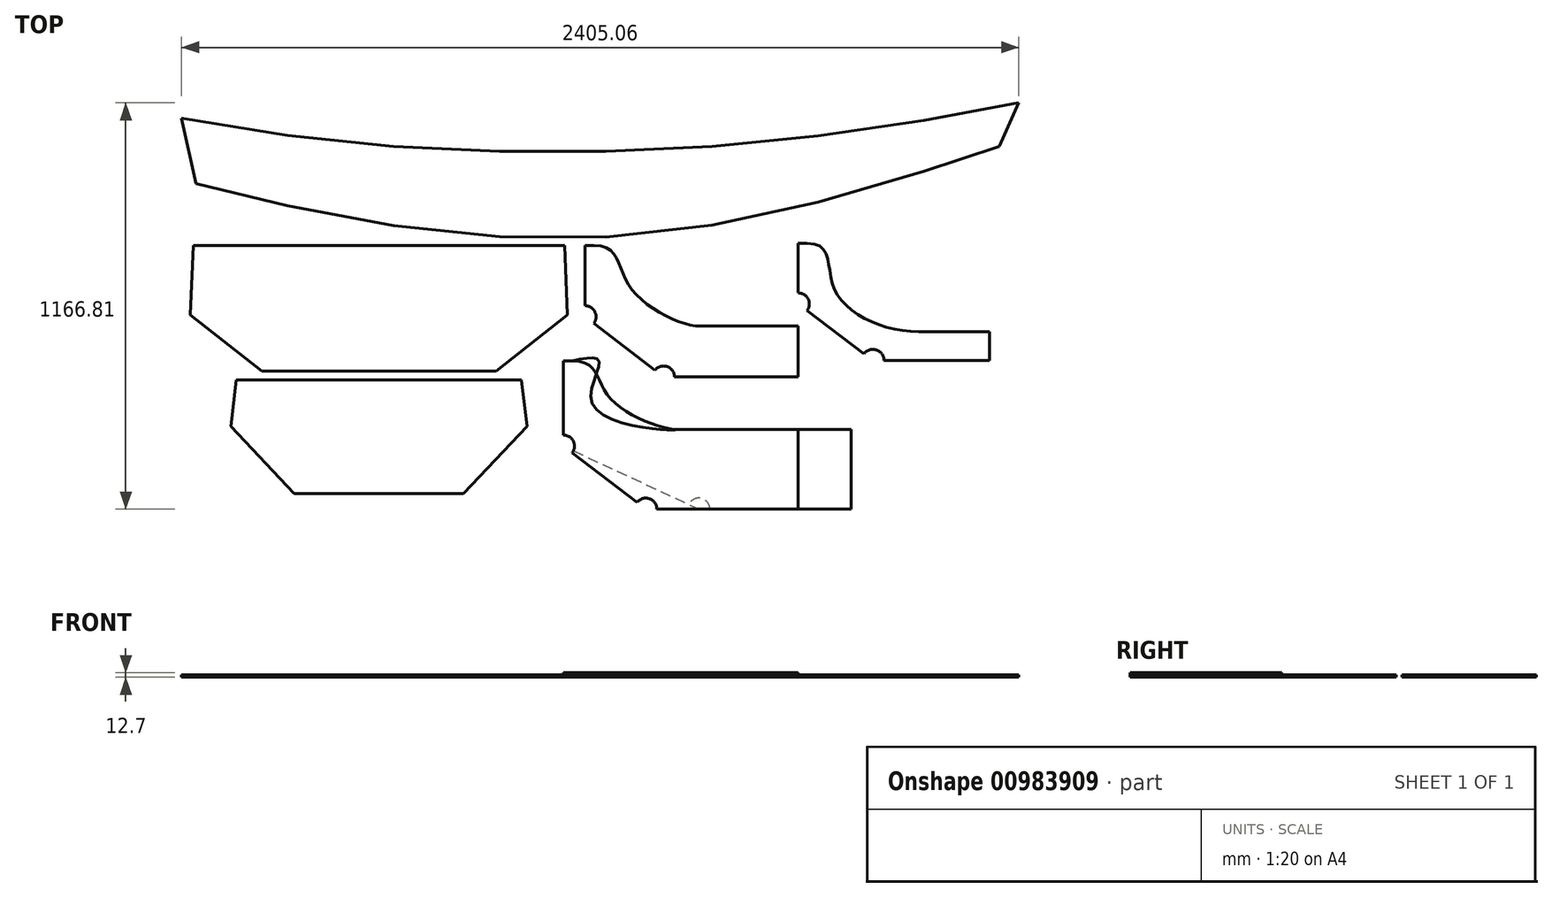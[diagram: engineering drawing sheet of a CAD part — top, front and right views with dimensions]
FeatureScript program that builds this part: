
annotation { "Feature Type Name" : "Feature", "Feature Type Description" : "" }
export const myFeature = defineFeature(function(context is Context, id is Id, definition is map)
    precondition{}
    {
        {
            var Q0;
            Q0=qCreatedBy(makeId("Top.planeOp"),FACE);
            var sketch = newSketch(context, id + "F0", { "sketchPlane" : qUnion([Q0])});
            skLineSegment(sketch, "E0.bottom", {"start": v(2438.4, -1219.2) * mm, "end": v(0, -1219.2) * mm});
            skLineSegment(sketch, "E0.top", {"start": v(2438.4, 0) * mm, "end": v(0, 0) * mm});
            skLineSegment(sketch, "E0.left", {"start": v(2438.4, -1219.2) * mm, "end": v(2438.4, 0) * mm});
            skLineSegment(sketch, "E0.right", {"start": v(0, -1219.2) * mm, "end": v(0, 0) * mm});
            skPoint(sketch, "E1", {"position": v(0, -44.45) * mm});
            skPoint(sketch, "E2", {"position": v(304.8, -93.66) * mm});
            skPoint(sketch, "E3", {"position": v(609.6, -125.41) * mm});
            skPoint(sketch, "E4", {"position": v(914.4, -139.7) * mm});
            skPoint(sketch, "E5", {"position": v(1219.2, -139.7) * mm});
            skPoint(sketch, "E6", {"position": v(1524, -125.41) * mm});
            skPoint(sketch, "E7", {"position": v(1828.8, -95.25) * mm});
            skPoint(sketch, "E8", {"position": v(2133.6, -50.8) * mm});
            skPoint(sketch, "E9", {"position": v(2405.06, 0) * mm});
            skLineSegment(sketch, "E10", {"start": v(2405.06, 0) * mm, "end": v(2133.6, -50.8) * mm});
            skLineSegment(sketch, "E11", {"start": v(1828.8, -95.25) * mm, "end": v(2133.6, -50.8) * mm});
            skLineSegment(sketch, "E12", {"start": v(1828.8, -95.25) * mm, "end": v(1524, -125.41) * mm});
            skLineSegment(sketch, "E13", {"start": v(1524, -125.41) * mm, "end": v(1219.2, -139.7) * mm});
            skLineSegment(sketch, "E14", {"start": v(914.4, -139.7) * mm, "end": v(1219.2, -139.7) * mm});
            skLineSegment(sketch, "E15", {"start": v(609.6, -125.41) * mm, "end": v(914.4, -139.7) * mm});
            skLineSegment(sketch, "E16", {"start": v(0, -44.45) * mm, "end": v(304.8, -93.66) * mm});
            skLineSegment(sketch, "E17", {"start": v(609.6, -125.41) * mm, "end": v(304.8, -93.66) * mm});
            skLineSegment(sketch, "E18", {"start": v(387.35, -102.26) * mm, "end": v(387.35, -310.75) * mm, "construction": true});
            skLineSegment(sketch, "E19", {"start": v(1079.5, -139.7) * mm, "end": v(1079.5, -385.03) * mm, "construction": true});
            skLineSegment(sketch, "E20", {"start": v(1909.76, -83.44) * mm, "end": v(1909.76, -262.14) * mm, "construction": true});
            skPoint(sketch, "E21", {"position": v(304.8, -295.27) * mm});
            skPoint(sketch, "E22", {"position": v(609.6, -352.42) * mm});
            skPoint(sketch, "E23", {"position": v(914.4, -384.17) * mm});
            skPoint(sketch, "E24", {"position": v(1219.2, -385.76) * mm});
            skPoint(sketch, "E25", {"position": v(1524, -350.84) * mm});
            skPoint(sketch, "E26", {"position": v(1828.8, -285.75) * mm});
            skPoint(sketch, "E27", {"position": v(2133.6, -196.85) * mm});
            skPoint(sketch, "E28", {"position": v(2349.5, -124.88) * mm});
            skPoint(sketch, "E29", {"position": v(41.27, -232.14) * mm});
            skPoint(sketch, "E30", {"position": v(0, -222.25) * mm});
            skLineSegment(sketch, "E31", {"start": v(304.8, -295.27) * mm, "end": v(609.6, -352.42) * mm});
            skLineSegment(sketch, "E32", {"start": v(609.6, -352.42) * mm, "end": v(914.4, -384.17) * mm});
            skLineSegment(sketch, "E33", {"start": v(914.4, -384.17) * mm, "end": v(1219.2, -385.76) * mm});
            skLineSegment(sketch, "E34", {"start": v(1219.2, -385.76) * mm, "end": v(1524, -350.84) * mm});
            skLineSegment(sketch, "E35", {"start": v(1524, -350.84) * mm, "end": v(1828.8, -285.75) * mm});
            skLineSegment(sketch, "E36", {"start": v(1828.8, -285.75) * mm, "end": v(2133.6, -196.85) * mm});
            skLineSegment(sketch, "E37", {"start": v(2133.6, -196.85) * mm, "end": v(2349.5, -124.88) * mm});
            skLineSegment(sketch, "E38", {"start": v(2349.5, -124.88) * mm, "end": v(2405.06, 0) * mm});
            skLineSegment(sketch, "E39.bottom", {"start": v(0, -1524) * mm, "end": v(2438.4, -1524) * mm});
            skLineSegment(sketch, "E39.top", {"start": v(0, -2743.2) * mm, "end": v(2438.4, -2743.2) * mm});
            skLineSegment(sketch, "E39.left", {"start": v(0, -1524) * mm, "end": v(0, -2743.2) * mm});
            skLineSegment(sketch, "E39.right", {"start": v(2438.4, -1524) * mm, "end": v(2438.4, -2743.2) * mm});
            skLineSegment(sketch, "E40", {"start": v(0, -1852.61) * mm, "end": v(2220.91, -1852.61) * mm, "construction": true});
            skPoint(sketch, "E41", {"position": v(0, -1665.29) * mm});
            skPoint(sketch, "E42", {"position": v(304.8, -1616.08) * mm});
            skPoint(sketch, "E43", {"position": v(609.6, -1581.15) * mm});
            skPoint(sketch, "E44", {"position": v(914.4, -1549.4) * mm});
            skPoint(sketch, "E45", {"position": v(1219.2, -1573.21) * mm});
            skPoint(sketch, "E46", {"position": v(1828.8, -1665.29) * mm});
            skPoint(sketch, "E47", {"position": v(1524, -1604.96) * mm});
            skLineSegment(sketch, "E48", {"start": v(0, -2005.01) * mm, "end": v(940, -2005.01) * mm, "construction": true});
            skPoint(sketch, "E49", {"position": v(2133.6, -1733.55) * mm});
            skPoint(sketch, "E50", {"position": v(2220.91, -1757.36) * mm});
            skPoint(sketch, "E51.MirrorP", {"position": v(0, -2344.74) * mm});
            skPoint(sketch, "E52.MirrorP", {"position": v(304.8, -2393.95) * mm});
            skPoint(sketch, "E53.MirrorP", {"position": v(609.6, -2428.87) * mm});
            skPoint(sketch, "E54.MirrorP", {"position": v(914.4, -2460.62) * mm});
            skPoint(sketch, "E55.MirrorP", {"position": v(1219.2, -2436.81) * mm});
            skPoint(sketch, "E56.MirrorP", {"position": v(1524, -2405.06) * mm});
            skPoint(sketch, "E57.MirrorP", {"position": v(1828.8, -2344.74) * mm});
            skPoint(sketch, "E58.MirrorP", {"position": v(2133.6, -2276.47) * mm});
            skPoint(sketch, "E59.MirrorP", {"position": v(2220.91, -2252.66) * mm});
            skLineSegment(sketch, "E60", {"start": v(0, -1665.29) * mm, "end": v(304.8, -1616.08) * mm});
            skLineSegment(sketch, "E61", {"start": v(304.8, -1616.08) * mm, "end": v(609.6, -1581.15) * mm});
            skLineSegment(sketch, "E62", {"start": v(609.6, -1581.15) * mm, "end": v(914.4, -1549.4) * mm});
            skLineSegment(sketch, "E63", {"start": v(914.4, -1549.4) * mm, "end": v(1219.2, -1573.21) * mm});
            skLineSegment(sketch, "E64", {"start": v(1524, -1604.96) * mm, "end": v(1219.2, -1573.21) * mm});
            skLineSegment(sketch, "E65", {"start": v(1828.8, -1665.29) * mm, "end": v(1524, -1604.96) * mm});
            skLineSegment(sketch, "E66", {"start": v(2133.6, -1733.55) * mm, "end": v(1828.8, -1665.29) * mm});
            skLineSegment(sketch, "E67", {"start": v(2220.91, -1757.36) * mm, "end": v(2133.6, -1733.55) * mm});
            skLineSegment(sketch, "E68", {"start": v(2220.91, -1757.36) * mm, "end": v(2220.91, -2252.66) * mm});
            skLineSegment(sketch, "E69", {"start": v(2133.6, -2276.47) * mm, "end": v(2220.91, -2252.66) * mm});
            skLineSegment(sketch, "E70", {"start": v(2133.6, -2276.47) * mm, "end": v(1828.8, -2344.74) * mm});
            skLineSegment(sketch, "E71", {"start": v(1524, -2405.06) * mm, "end": v(1828.8, -2344.74) * mm});
            skLineSegment(sketch, "E72", {"start": v(1524, -2405.06) * mm, "end": v(1219.2, -2436.81) * mm});
            skLineSegment(sketch, "E73", {"start": v(1219.2, -2436.81) * mm, "end": v(914.4, -2460.62) * mm});
            skLineSegment(sketch, "E74", {"start": v(914.4, -2460.62) * mm, "end": v(609.6, -2428.87) * mm});
            skLineSegment(sketch, "E75", {"start": v(609.6, -2428.87) * mm, "end": v(304.8, -2393.95) * mm});
            skLineSegment(sketch, "E76", {"start": v(304.8, -2393.95) * mm, "end": v(0, -2344.74) * mm});
            skLineSegment(sketch, "E77", {"start": v(33.34, -409.57) * mm, "end": v(25.4, -609.6) * mm});
            skLineSegment(sketch, "E78", {"start": v(25.4, -609.6) * mm, "end": v(230.19, -769.94) * mm});
            skLineSegment(sketch, "E79", {"start": v(230.19, -769.94) * mm, "end": v(566.74, -769.94) * mm});
            skLineSegment(sketch, "E80", {"start": v(566.74, -769.94) * mm, "end": v(566.74, -409.57) * mm, "construction": true});
            skLineSegment(sketch, "E81", {"start": v(414.34, -769.94) * mm, "end": v(414.34, -409.57) * mm, "construction": true});
            skLineSegment(sketch, "E82", {"start": v(33.34, -409.57) * mm, "end": v(566.74, -409.57) * mm});
            skLineSegment(sketch, "E83.MirrorCS", {"start": v(1100.14, -409.57) * mm, "end": v(1108.08, -609.6) * mm});
            skLineSegment(sketch, "E84.MirrorCS", {"start": v(1108.08, -609.6) * mm, "end": v(903.29, -769.94) * mm});
            skLineSegment(sketch, "E85.MirrorCS", {"start": v(903.29, -769.94) * mm, "end": v(566.74, -769.94) * mm});
            skLineSegment(sketch, "E86.MirrorCS", {"start": v(1100.14, -409.57) * mm, "end": v(566.74, -409.57) * mm});
            skLineSegment(sketch, "E87", {"start": v(566.74, -795.34) * mm, "end": v(157.16, -795.34) * mm});
            skLineSegment(sketch, "E88", {"start": v(157.16, -795.34) * mm, "end": v(141.29, -928.69) * mm});
            skLineSegment(sketch, "E89", {"start": v(141.29, -928.69) * mm, "end": v(323.85, -1122.36) * mm});
            skLineSegment(sketch, "E90", {"start": v(323.85, -1122.36) * mm, "end": v(566.74, -1122.36) * mm});
            skLineSegment(sketch, "E91.MirrorCS", {"start": v(809.62, -1122.36) * mm, "end": v(566.74, -1122.36) * mm});
            skLineSegment(sketch, "E92.MirrorCS", {"start": v(992.19, -928.69) * mm, "end": v(809.62, -1122.36) * mm});
            skLineSegment(sketch, "E93.MirrorCS", {"start": v(976.31, -795.34) * mm, "end": v(992.19, -928.69) * mm});
            skLineSegment(sketch, "E94.MirrorCS", {"start": v(566.74, -795.34) * mm, "end": v(976.31, -795.34) * mm});
            skLineSegment(sketch, "E95", {"start": v(41.27, -232.14) * mm, "end": v(0, -44.45) * mm});
            skLineSegment(sketch, "E96", {"start": v(0, -222.25) * mm, "end": v(41.27, -232.14) * mm, "construction": true});
            skLineSegment(sketch, "E97", {"start": v(41.27, -232.14) * mm, "end": v(304.8, -295.27) * mm});
            skLineSegment(sketch, "E98", {"start": v(2349.5, -124.88) * mm, "end": v(2405.06, -106.36) * mm, "construction": true});
            skLineSegment(sketch, "E99", {"start": v(1158.88, -409.57) * mm, "end": v(1158.88, -614.36) * mm});
            skLineSegment(sketch, "E100", {"start": v(1158.88, -614.36) * mm, "end": v(1384.3, -787.4) * mm});
            skLineSegment(sketch, "E101", {"start": v(1384.3, -787.4) * mm, "end": v(1771.65, -787.4) * mm});
            skLineSegment(sketch, "E102", {"start": v(1619.25, -582.61) * mm, "end": v(1619.25, -787.4) * mm, "construction": true});
            skLineSegment(sketch, "E103", {"start": v(1771.65, -787.4) * mm, "end": v(1771.65, -641.35) * mm});
            skLineSegment(sketch, "E104", {"start": v(1771.65, -641.35) * mm, "end": v(1489.08, -641.35) * mm});
            skLineSegment(sketch, "E105", {"start": v(1184.28, -409.57) * mm, "end": v(1158.88, -409.57) * mm});
            skLineSegment(sketch, "E106", {"start": v(1771.65, -1166.81) * mm, "end": v(1333.5, -1166.81) * mm});
            skLineSegment(sketch, "E107", {"start": v(1333.5, -1166.81) * mm, "end": v(1096.96, -985.84) * mm});
            skLineSegment(sketch, "E108", {"start": v(1096.96, -985.84) * mm, "end": v(1096.96, -741.36) * mm});
            skLineSegment(sketch, "E109", {"start": v(1771.65, -1166.81) * mm, "end": v(1771.65, -938.21) * mm});
            skLineSegment(sketch, "E110", {"start": v(1771.65, -938.21) * mm, "end": v(1427.16, -938.21) * mm});
            skLineSegment(sketch, "E111", {"start": v(1122.36, -741.36) * mm, "end": v(1096.96, -741.36) * mm});
            skLineSegment(sketch, "E112", {"start": v(1771.65, -403.06) * mm, "end": v(1771.65, -577.68) * mm});
            skLineSegment(sketch, "E113", {"start": v(1771.65, -577.68) * mm, "end": v(1985.96, -739.6) * mm});
            skLineSegment(sketch, "E114", {"start": v(1985.96, -739.6) * mm, "end": v(2320.93, -739.6) * mm});
            skLineSegment(sketch, "E115", {"start": v(2168.53, -739.6) * mm, "end": v(2168.53, -479.2) * mm, "construction": true});
            skLineSegment(sketch, "E116", {"start": v(2320.93, -739.6) * mm, "end": v(2320.93, -657.06) * mm});
            skLineSegment(sketch, "E117", {"start": v(2320.93, -657.06) * mm, "end": v(2117.72, -657.06) * mm});
            skLineSegment(sketch, "E118", {"start": v(1797.05, -403.06) * mm, "end": v(1771.65, -403.06) * mm});
            skLineSegment(sketch, "E119.bottom", {"start": v(2127.74, -949.56) * mm, "end": v(2280.14, -949.56) * mm});
            skLineSegment(sketch, "E119.top", {"start": v(2127.74, -1095.6) * mm, "end": v(2280.14, -1095.6) * mm});
            skLineSegment(sketch, "E119.left", {"start": v(2127.74, -949.56) * mm, "end": v(2127.74, -1095.6) * mm});
            skLineSegment(sketch, "E119.right", {"start": v(2280.14, -949.56) * mm, "end": v(2280.14, -1095.6) * mm});
            skLineSegment(sketch, "E120.bottom", {"start": v(2156.03, -808.16) * mm, "end": v(2359.23, -808.16) * mm});
            skLineSegment(sketch, "E120.top", {"start": v(2156.03, -890.71) * mm, "end": v(2359.23, -890.71) * mm});
            skLineSegment(sketch, "E120.left", {"start": v(2156.03, -808.16) * mm, "end": v(2156.03, -890.71) * mm});
            skLineSegment(sketch, "E120.right", {"start": v(2359.23, -808.16) * mm, "end": v(2359.23, -890.71) * mm});
            skLineSegment(sketch, "E121", {"start": v(1771.65, -938.21) * mm, "end": v(1771.65, -858.32) * mm, "construction": true});
            skLineSegment(sketch, "E122", {"start": v(1065.21, -709.3) * mm, "end": v(1065.21, -838.62) * mm});
            skFitSpline(sketch, "E123", {"points": [v(2117.73, -657.06) * mm, v(1873.25, -530.06) * mm, v(1797.05, -403.06) * mm], "startDerivative": vector(-528.28, 0) * mm, "endDerivative": vector(-540.38, 0) * mm});
            skFitSpline(sketch, "E124", {"points": [v(1184.28, -409.57) * mm, v(1285.87, -525.46) * mm, v(1489.07, -641.35) * mm], "startDerivative": vector(510.23, 0) * mm, "endDerivative": vector(276.1, 0) * mm});
            skFitSpline(sketch, "E125", {"points": [v(1122.36, -741.36) * mm, v(1223.96, -839.79) * mm, v(1427.16, -938.21) * mm], "startDerivative": vector(517.4, 0) * mm, "endDerivative": vector(273.03, 0) * mm});
            skLineSegment(sketch, "E126", {"start": v(1223.96, -741.36) * mm, "end": v(1223.96, -938.21) * mm, "construction": true});
            skLineSegment(sketch, "E127", {"start": v(1285.88, -409.57) * mm, "end": v(1285.88, -641.35) * mm, "construction": true});
            skLineSegment(sketch, "E128", {"start": v(1873.25, -403.06) * mm, "end": v(1873.25, -657.06) * mm, "construction": true});
            skArc(sketch, "E129", {"start": v(1416.05, -787.4) * mm, "mid": v(1394.5, -757.34) * mm, "end": v(1359.11, -768.07) * mm});
            skArc(sketch, "E130", {"start": v(1184.06, -633.7) * mm, "mid": v(1187.35, -600.32) * mm, "end": v(1158.88, -582.61) * mm});
            skArc(sketch, "E131", {"start": v(1365.25, -1166.81) * mm, "mid": v(1343.68, -1136.74) * mm, "end": v(1308.28, -1147.52) * mm});
            skArc(sketch, "E132", {"start": v(1771.65, -545.93) * mm, "mid": v(1800.07, -563.53) * mm, "end": v(1796.98, -596.82) * mm});
            skArc(sketch, "E133", {"start": v(1960.63, -720.47) * mm, "mid": v(1996.06, -709.5) * mm, "end": v(2017.71, -739.6) * mm});
            skLineSegment(sketch, "E134", {"start": v(1836.14, -528.11) * mm, "end": v(1992.31, -646.1) * mm, "construction": true});
            skArc(sketch, "E135", {"start": v(1096.96, -954.09) * mm, "mid": v(1125.43, -971.77) * mm, "end": v(1122.18, -1005.13) * mm});
            skLineSegment(sketch, "E136", {"start": v(1096.96, -985.84) * mm, "end": v(1485.9, -1166.81) * mm});
            skLineSegment(sketch, "E137.bottom", {"start": v(1771.65, -938.21) * mm, "end": v(1924.05, -938.21) * mm});
            skLineSegment(sketch, "E137.top", {"start": v(1771.65, -1166.81) * mm, "end": v(1924.05, -1166.81) * mm});
            skLineSegment(sketch, "E137.left", {"start": v(1771.65, -938.21) * mm, "end": v(1771.65, -1166.81) * mm});
            skLineSegment(sketch, "E137.right", {"start": v(1924.05, -938.21) * mm, "end": v(1924.05, -1166.81) * mm});
            skArc(sketch, "E138", {"start": v(1517.65, -1166.81) * mm, "mid": v(1492.76, -1135.81) * mm, "end": v(1457.11, -1153.42) * mm});
            skSolve(sketch);
        }
        {
            var Q0;
            {var subQ0=sQuery(id+"F0.wireOp",EDGE,"E103");Q0=makeQuery(id+"F0.imprint","IMPRINT",FACE,{"disambiguationData":[TD([[makeQuery(id+"F0.imprint","IMPRINT",EDGE,{"derivedFrom":subQ0}),1.0]])]});}
            var Q1;
            {var subQ0=sQuery(id+"F0.wireOp",EDGE,"E109");Q1=makeQuery(id+"F0.imprint","IMPRINT",FACE,{"disambiguationData":[TD([[makeQuery(id+"F0.imprint","IMPRINT",EDGE,{"derivedFrom":subQ0}),1.0]])]});}
            var Q2;
            {var subQ0=sQuery(id+"F0.wireOp",EDGE,"E116");Q2=makeQuery(id+"F0.imprint","IMPRINT",FACE,{"disambiguationData":[TD([[makeQuery(id+"F0.imprint","IMPRINT",EDGE,{"derivedFrom":subQ0}),1.0]])]});}
            var Q3;
            Q3=makeQuery(id+"F0.imprint","IMPRINT",FACE,{"disambiguationData":[TD([[makeQuery(id+"F0.imprint","IMPRINT",EDGE,{"derivedFrom":sQuery(id+"F0.wireOp",EDGE,"E87")}),1.0]])]});
            var Q4;
            Q4=makeQuery(id+"F0.imprint","IMPRINT",FACE,{"disambiguationData":[TD([[makeQuery(id+"F0.imprint","IMPRINT",EDGE,{"derivedFrom":sQuery(id+"F0.wireOp",EDGE,"E77")}),1.0]])]});
            var Q5;
            Q5=makeQuery(id+"F0.imprint","IMPRINT",FACE,{"disambiguationData":[TD([[makeQuery(id+"F0.imprint","IMPRINT",EDGE,{"derivedFrom":sQuery(id+"F0.wireOp",EDGE,"E10")}),1.0]])]});
            var Q6;
            Q6=makeQuery(id+"F0.imprint","IMPRINT",FACE,{"disambiguationData":[TD([[makeQuery(id+"F0.imprint","IMPRINT",EDGE,{"derivedFrom":sQuery(id+"F0.wireOp",EDGE,"E110")}),1.0]])]});
            extrude(context, id + "F1", {"entities" : qUnion([Q0, Q1, Q2, Q3, Q4, Q5, Q6]), "depth" : 6.35 * mm, "offsetDistance" : 25.4 * mm});
        }
        {
            var Q0;
            {var subQ5=sQuery(id+"F0.wireOp",EDGE,"E131");Q0=makeQuery(id+"F0.imprint","IMPRINT",FACE,{"disambiguationData":[TD([[makeQuery(id+"F0.imprint","IMPRINT",EDGE,{"derivedFrom":subQ5}),-1.0]])]});}
            var Q1;
            Q1=makeQuery(id+"F0.imprint","IMPRINT",FACE,{"disambiguationData":[TD([[makeQuery(id+"F0.imprint","IMPRINT",EDGE,{"derivedFrom":sQuery(id+"F0.wireOp",EDGE,"E137.bottom")}),-1.0]])]});
            extrude(context, id + "F2", {"entities" : qUnion([Q0, Q1]), "depth" : 6.35 * mm, "offsetDistance" : 25.4 * mm});
        }
        {
            var Q0;
            Q0=makeQuery(id+"F1.opExtrude","CAP_FACE",FACE,{"disambiguationData":[OSD([sQuery(id+"F0.wireOp",EDGE,"E106"),sQuery(id+"F0.wireOp",EDGE,"E108"),sQuery(id+"F0.wireOp",EDGE,"E110"),sQuery(id+"F0.wireOp",EDGE,"E111"),sQuery(id+"F0.wireOp",EDGE,"E125"),sQuery(id+"F0.wireOp",EDGE,"E135"),sQuery(id+"F0.wireOp",EDGE,"E136"),sQuery(id+"F0.wireOp",EDGE,"E137.left"),sQuery(id+"F0.wireOp",EDGE,"E138")])],"isStart":false});
            var sketch = newSketch(context, id + "F3", { "sketchPlane" : qUnion([Q0])});
            skLineSegment(sketch, "E139", {"start": v(1125.75, -999.23) * mm, "end": v(1577.12, -1166.81) * mm});
            skLineSegment(sketch, "E140", {"start": v(1125.75, -999.23) * mm, "end": v(1096.08, -988.22) * mm});
            skLineSegment(sketch, "E141", {"start": v(1096.08, -988.22) * mm, "end": v(1108.01, -956.07) * mm});
            skLineSegment(sketch, "E142", {"start": v(1108.01, -956.07) * mm, "end": v(1675.63, -1166.81) * mm});
            skLineSegment(sketch, "E143.0", {"start": v(1771.65, -1166.81) * mm, "end": v(1517.65, -1166.81) * mm});
            skPoint(sketch, "E144", {"position": v(1333.5, -1166.81) * mm});
            skSolve(sketch);
        }
        {
            var Q0;
            {var subQ3=sQuery(id+"F3.wireOp",EDGE,"E142");Q0=makeQuery(id+"F3.imprint","IMPRINT",FACE,{"disambiguationData":[TD([[makeQuery(id+"F3.imprint","IMPRINT",EDGE,{"derivedFrom":subQ3}),1.0]])]});}
            var sketch = newSketch(context, id + "F4", { "sketchPlane" : qUnion([Q0])});
            skLineSegment(sketch, "E145.0", {"start": v(1096.96, -954.09) * mm, "end": v(1096.96, -741.36) * mm});
            skLineSegment(sketch, "E146.0", {"start": v(1122.36, -741.36) * mm, "end": v(1096.96, -741.36) * mm});
            skFitSpline(sketch, "E146.1", {"points": [v(1122.36, -741.36) * mm, v(1198.56, -741.36) * mm, v(1179.7, -863) * mm, v(1376.36, -938.21) * mm, v(1427.16, -938.21) * mm]});
            skLineSegment(sketch, "E147.0", {"start": v(1771.65, -938.21) * mm, "end": v(1427.16, -938.21) * mm});
            skLineSegment(sketch, "E148.0", {"start": v(1771.65, -938.21) * mm, "end": v(1771.65, -1166.81) * mm});
            skLineSegment(sketch, "E149.0", {"start": v(1771.65, -1166.81) * mm, "end": v(1517.65, -1166.81) * mm});
            skLineSegment(sketch, "E150.0", {"start": v(1485.9, -1166.81) * mm, "end": v(1365.25, -1166.81) * mm});
            skLineSegment(sketch, "E151", {"start": v(1485.9, -1166.81) * mm, "end": v(1517.65, -1166.81) * mm});
            skArc(sketch, "E152.0", {"start": v(1365.25, -1166.81) * mm, "mid": v(1343.68, -1136.74) * mm, "end": v(1308.28, -1147.52) * mm});
            skLineSegment(sketch, "E152.1", {"start": v(1308.28, -1147.52) * mm, "end": v(1122.18, -1005.13) * mm});
            skArc(sketch, "E153.0", {"start": v(1096.96, -954.09) * mm, "mid": v(1123.73, -968.77) * mm, "end": v(1125.75, -999.23) * mm});
            skArc(sketch, "E154.0", {"start": v(1125.75, -999.23) * mm, "mid": v(1124.12, -1002.28) * mm, "end": v(1122.18, -1005.13) * mm});
            skSolve(sketch);
        }
        {
            var Q0;
            Q0 = qSketchRegion(id + "F4", true);
            extrude(context, id + "F5", {"entities" : qUnion([Q0]), "depth" : 6.35 * mm, "offsetDistance" : 25.4 * mm});
        }
    });
